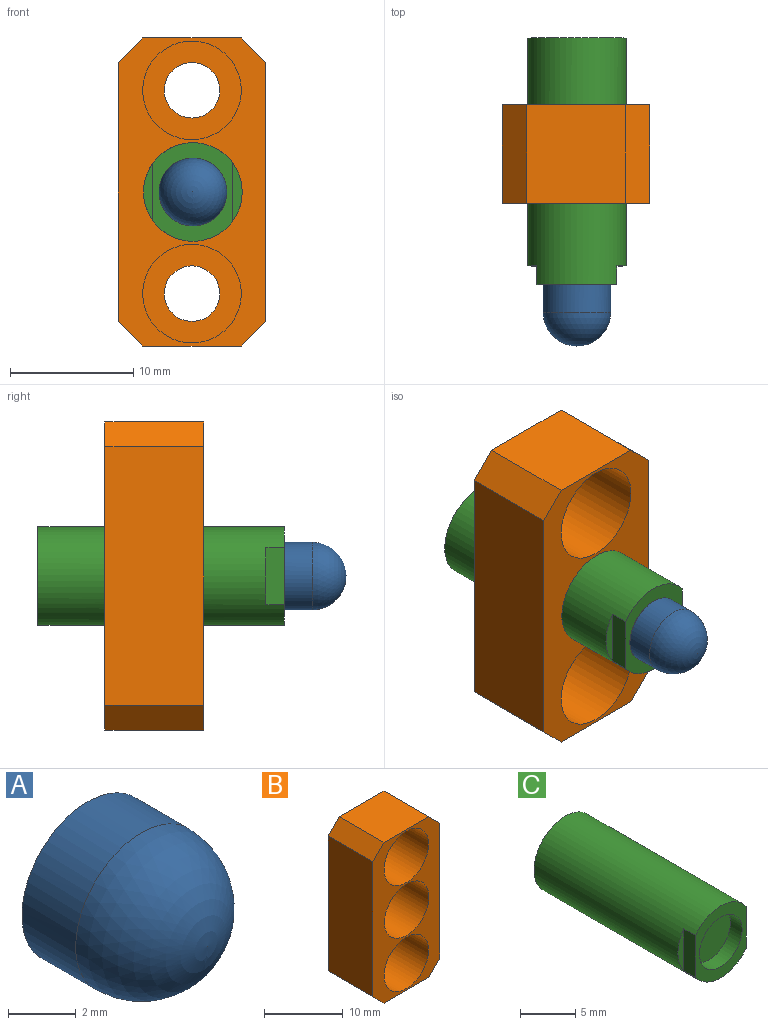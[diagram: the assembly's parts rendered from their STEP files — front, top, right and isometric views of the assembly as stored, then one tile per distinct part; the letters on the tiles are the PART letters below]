
ASSEMBLY  parts=3 mates=3
PART A: 3 faces, bbox 5.5x5x5.5 mm
  f0: sphere r=2.75mm, area 47.5mm2, adj f1
  f1: cylinder r=2.75mm len=5.5mm, axis (0,-1,0), area 38.9mm2, adj f0,f2
  f2: plane 5.5x5.5mm, normal (0,1,0), area 23.8mm2, adj f1
PART B: 17 faces, bbox 12x8x25 mm
  f0: cylinder r=2.25mm len=4.5mm, axis (0,-1,0), area 14.1mm2, adj f7,f14
  f1: cylinder r=2.25mm len=4.5mm, axis (0,-1,0), area 14.1mm2, adj f7,f12
  f2: plane 21x8mm, normal (-1,0,0), area 168mm2, adj f6,f7,f8,f9
  f3: plane 8x8mm, normal (0,0,-1), area 64mm2, adj f6,f7,f9,f10
  f4: plane 21x8mm, normal (1,0,0), area 168mm2, adj f6,f7,f10,f11
  f5: plane 8x8mm, normal (0,0,1), area 64mm2, adj f6,f7,f8,f11
  f6: plane 25x12mm, normal (0,-1,0), area 141.2mm2, adj f2,f3,f4,f5,f8,f9,f10,f11
  f7: plane 25x12mm, normal (0,1,0), area 209.9mm2, adj f0,f1,f2,f3,f4,f5,f8,f9
  f8: plane 8x2mm, normal (-0.71,0,0.71), area 22.6mm2, adj f2,f5,f6,f7
  f9: plane 8x2mm, normal (-0.71,0,-0.71), area 22.6mm2, adj f2,f3,f6,f7
  f10: plane 8x2mm, normal (0.71,0,-0.71), area 22.6mm2, adj f3,f4,f6,f7
  f11: plane 8x2mm, normal (0.71,0,0.71), area 22.6mm2, adj f4,f5,f6,f7
  f12: plane 8x8mm, normal (0,-1,0), area 34.4mm2, adj f1,f13
  f13: cylinder r=4mm len=8mm, axis (0,-1,0), area 175.9mm2, adj f6,f12
  f14: plane 8x8mm, normal (0,-1,0), area 34.4mm2, adj f0,f15
  f15: cylinder r=4mm len=8mm, axis (0,-1,0), area 175.9mm2, adj f6,f14
  f16: cylinder r=4mm len=8mm, axis (0,1,0), area 201.1mm2, adj f6,f7
PART C: 9 faces, bbox 8x20x8 mm
  f0: plane 8x6.5mm, normal (0,-1,0), area 21.7mm2, adj f1,f3,f5,f7
  f1: cylinder r=4mm len=20mm, axis (0,1,0), area 487.7mm2, adj f0,f2,f5,f6,f7,f8
  f2: plane 8x8mm, normal (0,1,0), area 50.3mm2, adj f1
  f3: cylinder r=2.75mm len=5.5mm, axis (0,-1,0), area 25.9mm2, adj f0,f4
  f4: plane 5.5x5.5mm, normal (0,-1,0), area 23.8mm2, adj f3
  f5: plane 4.66x1.5mm, normal (-1,0,0), area 7mm2, adj f0,f1,f6
  f6: plane 4.66x0.75mm, normal (0,-1,0), area 2.4mm2, adj f1,f5
  f7: plane 4.66x1.5mm, normal (1,0,0), area 7mm2, adj f0,f1,f8
  f8: plane 4.66x0.75mm, normal (0,-1,0), area 2.4mm2, adj f1,f7
PLACE A t=(-5.4,7.03,0.66)mm
PLACE B t=(-7.29,1.59,-2.61)mm
PLACE C t=(-5.4,7.03,0.66)mm
MATE planar A.f1 <-> C.f1  axis (0,1,0) through (-5.4,-12.97,0.66)mm
MATE slider A.f1 <-> C.f1  axis (0,-1,0) through (-5.4,-14.1,0.66)mm
MATE slider C.f1 <-> B.f16  axis (0,1,0) through (-5.4,-2.97,0.66)mm
